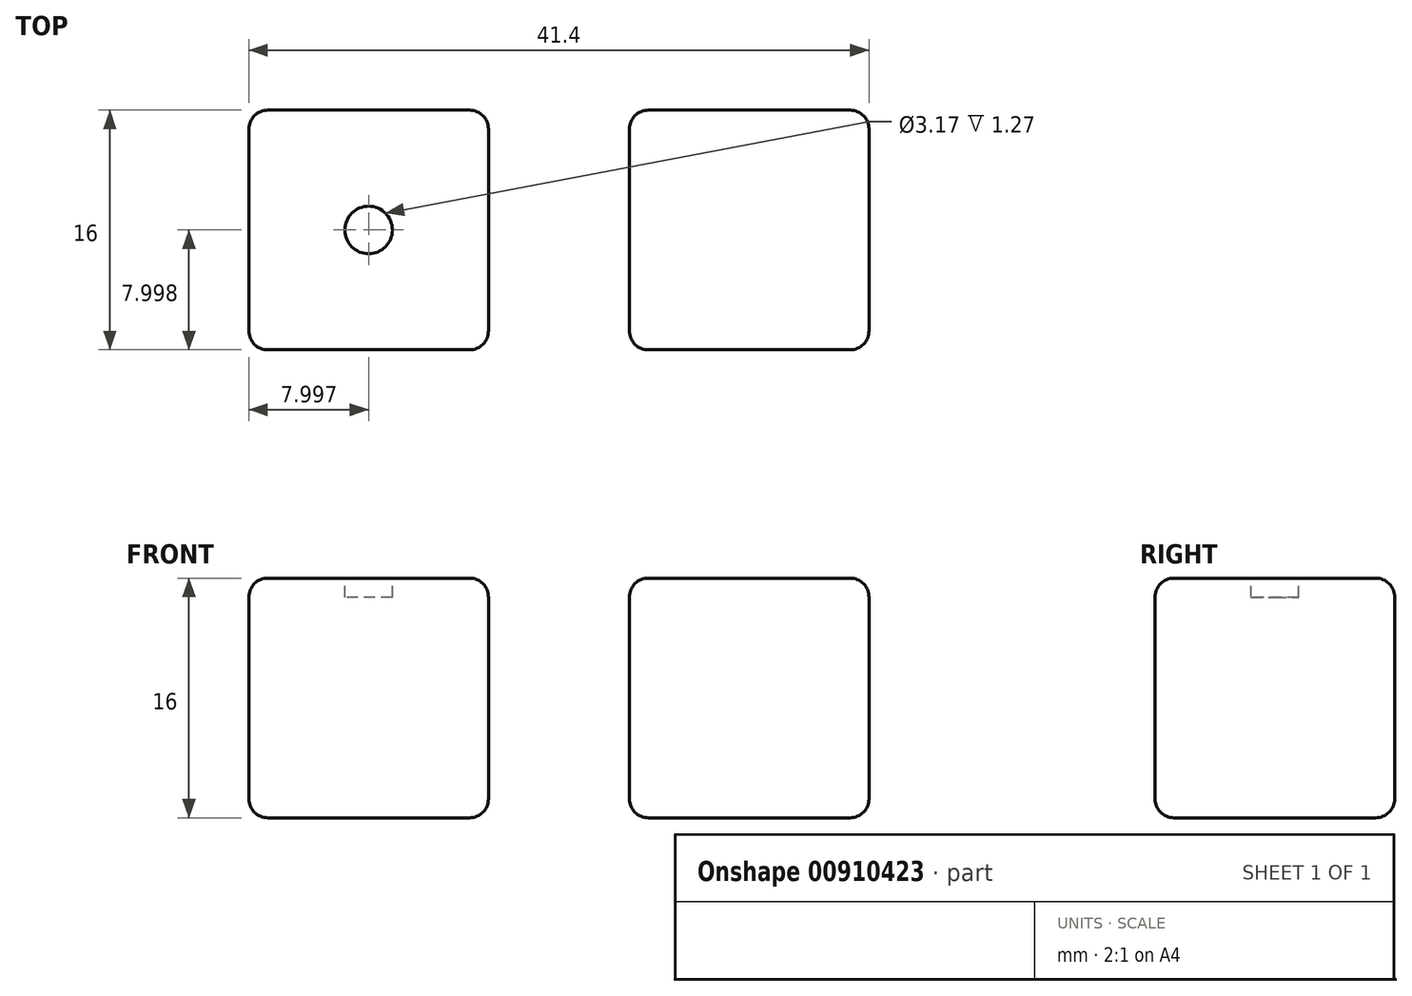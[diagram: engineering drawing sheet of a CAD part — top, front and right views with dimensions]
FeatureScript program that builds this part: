
annotation { "Feature Type Name" : "Feature", "Feature Type Description" : "" }
export const myFeature = defineFeature(function(context is Context, id is Id, definition is map)
    precondition{}
    {
        {
            assignVariable(context, id + "F0", {"name" : "length", "anyValue" : 16 * mm});
        }
        {
            var Q0;
            Q0=qCreatedBy(makeId("Top.planeOp"),FACE);
            var sketch = newSketch(context, id + "F1", { "sketchPlane" : qUnion([Q0])});
            skLineSegment(sketch, "E0.bottom", {"start": v(-39.15, 14.8) * mm, "end": v(-23.15, 14.8) * mm});
            skLineSegment(sketch, "E0.top", {"start": v(-39.15, -1.2) * mm, "end": v(-23.15, -1.2) * mm});
            skLineSegment(sketch, "E0.left", {"start": v(-39.15, 14.8) * mm, "end": v(-39.15, -1.2) * mm});
            skLineSegment(sketch, "E0.right", {"start": v(-23.15, 14.8) * mm, "end": v(-23.15, -1.2) * mm});
            skLineSegment(sketch, "E1.1.0.0", {"start": v(2.25, 14.8) * mm, "end": v(2.25, -1.2) * mm});
            skLineSegment(sketch, "E1.1.0.1", {"start": v(-13.75, 14.8) * mm, "end": v(-13.75, -1.2) * mm});
            skLineSegment(sketch, "E1.1.0.2", {"start": v(-13.75, -1.2) * mm, "end": v(2.25, -1.2) * mm});
            skLineSegment(sketch, "E1.1.0.3", {"start": v(-13.75, 14.8) * mm, "end": v(2.25, 14.8) * mm});
            skLineSegment(sketch, "E1.direction1", {"start": v(-39.15, -1.2) * mm, "end": v(-13.75, -1.2) * mm, "construction": true});
            skSolve(sketch);
        }
        {
            var Q0;
            Q0=qSketchRegion(id+"F1",true);
            extrude(context, id + "F2", {"entities" : qUnion([Q0]), "depth" : getVariable(context, 'length'), "offsetDistance" : 25.4 * mm});
        }
        {
            var Q0;
            Q0=makeQuery(id+"F2.opExtrude","CAP_EDGE",EDGE,{"disambiguationData":[OSD([sQuery(id+"F1.wireOp",EDGE,"E0.right")])],"isStart":true});
            var Q1;
            Q1=makeQuery(id+"F2.opExtrude","CAP_EDGE",EDGE,{"disambiguationData":[OSD([sQuery(id+"F1.wireOp",EDGE,"E0.left")])],"isStart":false});
            var Q2;
            Q2=makeQuery(id+"F2.opExtrude","CAP_EDGE",EDGE,{"disambiguationData":[OSD([sQuery(id+"F1.wireOp",EDGE,"E0.top")])],"isStart":false});
            var Q3;
            Q3=makeQuery(id+"F2.opExtrude","SWEPT_EDGE",EDGE,{"disambiguationData":[OSD([sQuery(id+"F1.wireOp",EDGE,"E0.bottom"),sQuery(id+"F1.wireOp",EDGE,"E0.right")])]});
            var Q4;
            Q4=makeQuery(id+"F2.opExtrude","SWEPT_EDGE",EDGE,{"disambiguationData":[OSD([sQuery(id+"F1.wireOp",EDGE,"E0.top"),sQuery(id+"F1.wireOp",EDGE,"E0.right")])]});
            var Q5;
            Q5=makeQuery(id+"F2.opExtrude","CAP_EDGE",EDGE,{"disambiguationData":[OSD([sQuery(id+"F1.wireOp",EDGE,"E0.bottom")])],"isStart":false});
            var Q6;
            Q6=makeQuery(id+"F2.opExtrude","SWEPT_EDGE",EDGE,{"disambiguationData":[OSD([sQuery(id+"F1.wireOp",EDGE,"E0.top"),sQuery(id+"F1.wireOp",EDGE,"E0.left")])]});
            var Q7;
            Q7=makeQuery(id+"F2.opExtrude","CAP_EDGE",EDGE,{"disambiguationData":[OSD([sQuery(id+"F1.wireOp",EDGE,"E0.right")])],"isStart":false});
            var Q8;
            Q8=makeQuery(id+"F2.opExtrude","CAP_EDGE",EDGE,{"disambiguationData":[OSD([sQuery(id+"F1.wireOp",EDGE,"E0.top")])],"isStart":true});
            var Q9;
            Q9=makeQuery(id+"F2.opExtrude","CAP_EDGE",EDGE,{"disambiguationData":[OSD([sQuery(id+"F1.wireOp",EDGE,"E1.1.0.2")])],"isStart":true});
            var Q10;
            Q10=makeQuery(id+"F2.opExtrude","CAP_EDGE",EDGE,{"disambiguationData":[OSD([sQuery(id+"F1.wireOp",EDGE,"E1.1.0.0")])],"isStart":true});
            var Q11;
            Q11=makeQuery(id+"F2.opExtrude","SWEPT_EDGE",EDGE,{"disambiguationData":[OSD([sQuery(id+"F1.wireOp",EDGE,"E1.1.0.1"),sQuery(id+"F1.wireOp",EDGE,"E1.1.0.2")])]});
            var Q12;
            Q12=makeQuery(id+"F2.opExtrude","CAP_EDGE",EDGE,{"disambiguationData":[OSD([sQuery(id+"F1.wireOp",EDGE,"E1.1.0.2")])],"isStart":false});
            var Q13;
            Q13=makeQuery(id+"F2.opExtrude","SWEPT_EDGE",EDGE,{"disambiguationData":[OSD([sQuery(id+"F1.wireOp",EDGE,"E1.1.0.0"),sQuery(id+"F1.wireOp",EDGE,"E1.1.0.2")])]});
            var Q14;
            Q14=makeQuery(id+"F2.opExtrude","SWEPT_EDGE",EDGE,{"disambiguationData":[OSD([sQuery(id+"F1.wireOp",EDGE,"E1.1.0.0"),sQuery(id+"F1.wireOp",EDGE,"E1.1.0.3")])]});
            var Q15;
            Q15=makeQuery(id+"F2.opExtrude","CAP_EDGE",EDGE,{"disambiguationData":[OSD([sQuery(id+"F1.wireOp",EDGE,"E1.1.0.1")])],"isStart":false});
            var Q16;
            Q16=makeQuery(id+"F2.opExtrude","CAP_EDGE",EDGE,{"disambiguationData":[OSD([sQuery(id+"F1.wireOp",EDGE,"E1.1.0.3")])],"isStart":false});
            var Q17;
            Q17=makeQuery(id+"F2.opExtrude","CAP_EDGE",EDGE,{"disambiguationData":[OSD([sQuery(id+"F1.wireOp",EDGE,"E1.1.0.0")])],"isStart":false});
            var Q18;
            Q18=makeQuery(id+"F2.opExtrude","SWEPT_EDGE",EDGE,{"disambiguationData":[OSD([sQuery(id+"F1.wireOp",EDGE,"E0.bottom"),sQuery(id+"F1.wireOp",EDGE,"E0.left")])]});
            var Q19;
            Q19=makeQuery(id+"F2.opExtrude","CAP_EDGE",EDGE,{"disambiguationData":[OSD([sQuery(id+"F1.wireOp",EDGE,"E0.left")])],"isStart":true});
            var Q20;
            Q20=makeQuery(id+"F2.opExtrude","CAP_EDGE",EDGE,{"disambiguationData":[OSD([sQuery(id+"F1.wireOp",EDGE,"E0.bottom")])],"isStart":true});
            var Q21;
            Q21=makeQuery(id+"F2.opExtrude","CAP_EDGE",EDGE,{"disambiguationData":[OSD([sQuery(id+"F1.wireOp",EDGE,"E1.1.0.1")])],"isStart":true});
            var Q22;
            Q22=makeQuery(id+"F2.opExtrude","CAP_EDGE",EDGE,{"disambiguationData":[OSD([sQuery(id+"F1.wireOp",EDGE,"E1.1.0.3")])],"isStart":true});
            var Q23;
            Q23=makeQuery(id+"F2.opExtrude","SWEPT_EDGE",EDGE,{"disambiguationData":[OSD([sQuery(id+"F1.wireOp",EDGE,"E1.1.0.1"),sQuery(id+"F1.wireOp",EDGE,"E1.1.0.3")])]});
            fillet(context, id + "F3", {"entities" : qUnion([Q0, Q1, Q2, Q3, Q4, Q5, Q6, Q7, Q8, Q9, Q10, Q11, Q12, Q13, Q14, Q15, Q16, Q17, Q18, Q19, Q20, Q21, Q22, Q23]), "radius" : 1.27 * mm, "tangentPropagation" : true, "allowEdgeOverflow" : false});
        }
        {
            var Q0;
            Q0=makeQuery(id+"F2.opExtrude","CAP_FACE",FACE,{"disambiguationData":[OSD([sQuery(id+"F1.wireOp",EDGE,"E0.bottom"),sQuery(id+"F1.wireOp",EDGE,"E0.top"),sQuery(id+"F1.wireOp",EDGE,"E0.left"),sQuery(id+"F1.wireOp",EDGE,"E0.right")])],"isStart":false});
            var sketch = newSketch(context, id + "F4", { "sketchPlane" : qUnion([Q0])});
            skCircle(sketch, "E2", {"center": v(-31.15, 6.8) * mm, "radius": 1.59 * mm});
            skPoint(sketch, "E2.centerSnap0", {"position": v(-31.15, 13.54) * mm});
            skPoint(sketch, "E2.centerSnap1", {"position": v(-37.88, 6.8) * mm});
            skSolve(sketch);
        }
        {
            var Q0;
            Q0=makeQuery(id+"F4.imprint","IMPRINT",FACE,{"disambiguationData":[TD([[makeQuery(id+"F4.imprint","IMPRINT",EDGE,{"derivedFrom":sQuery(id+"F4.wireOp",EDGE,"E2")}),1.0]])]});
            extrude(context, id + "F5", {"entities" : qUnion([Q0]), "operationType" : NewBodyOperationType.REMOVE, "oppositeDirection" : true, "depth" : 1.27 * mm, "offsetDistance" : 25.4 * mm});
        }
    });
